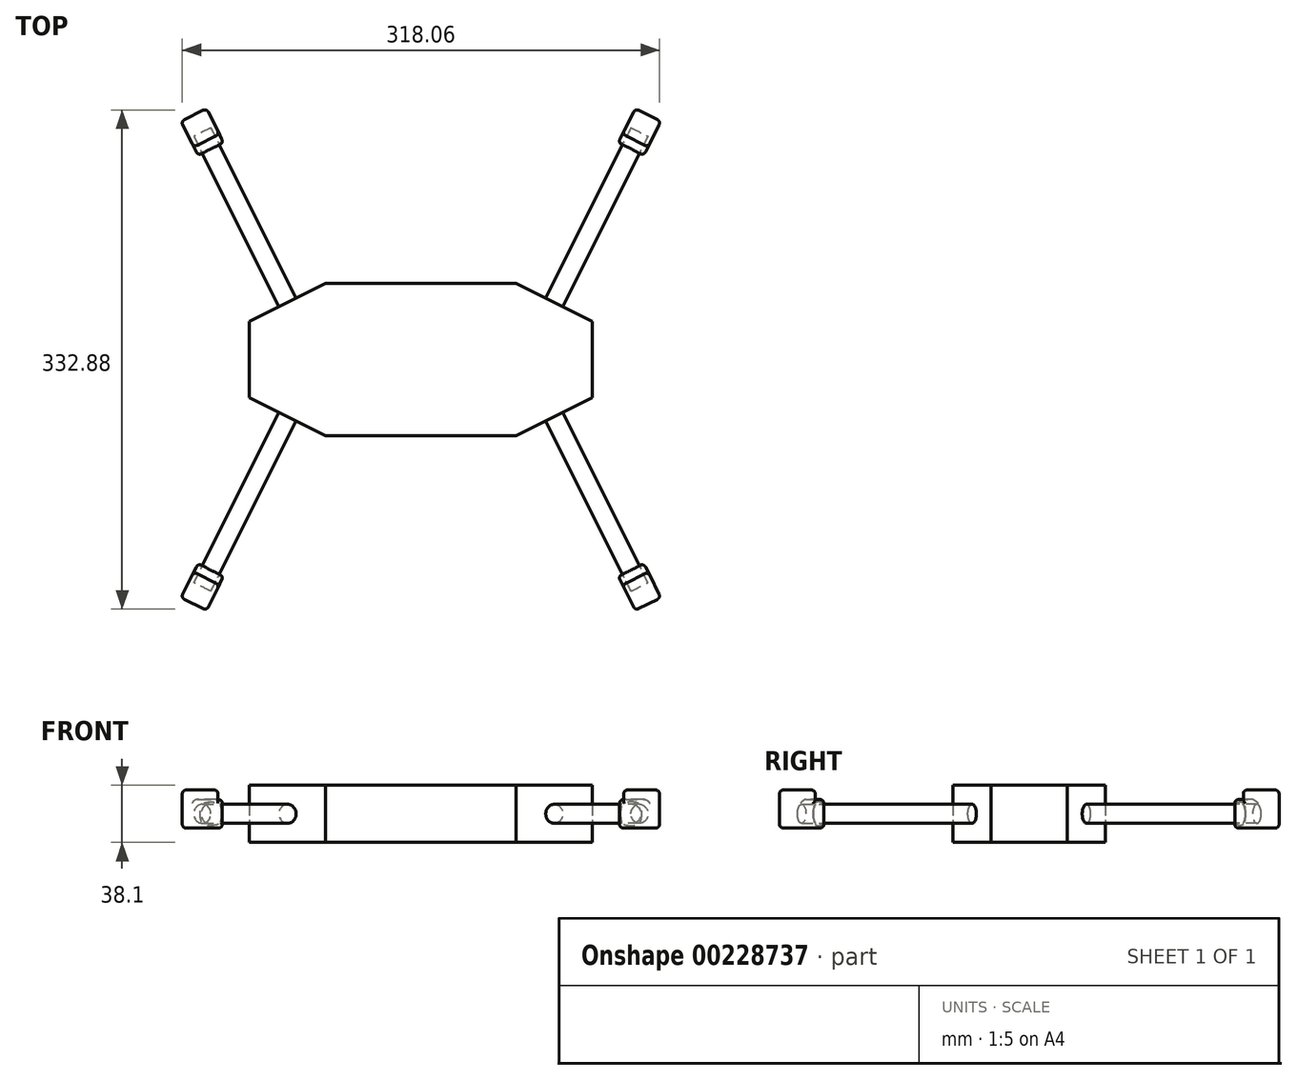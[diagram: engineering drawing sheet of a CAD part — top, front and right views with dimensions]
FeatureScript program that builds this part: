
annotation { "Feature Type Name" : "Feature", "Feature Type Description" : "" }
export const myFeature = defineFeature(function(context is Context, id is Id, definition is map)
    precondition{}
    {
        {
            var Q0;
            Q0=qCreatedBy(makeId("Top.planeOp"),FACE);
            var sketch = newSketch(context, id + "F0", { "sketchPlane" : qUnion([Q0])});
            skLineSegment(sketch, "E0.left", {"start": v(-114.3, 25.4) * mm, "end": v(-114.3, -25.4) * mm});
            skPoint(sketch, "E0.middle", {"position": v(0, 0) * mm});
            skLineSegment(sketch, "E1", {"start": v(-63.5, 50.8) * mm, "end": v(-114.3, 25.4) * mm});
            skLineSegment(sketch, "E2", {"start": v(-114.3, -25.4) * mm, "end": v(-63.5, -50.8) * mm});
            skLineSegment(sketch, "E3", {"start": v(0, 74.05) * mm, "end": v(0, -66) * mm, "construction": true});
            skLineSegment(sketch, "E4", {"start": v(-63.5, 50.8) * mm, "end": v(63.5, 50.8) * mm});
            skLineSegment(sketch, "E5", {"start": v(63.5, -50.8) * mm, "end": v(-63.5, -50.8) * mm});
            skLineSegment(sketch, "E6.MirrorCS", {"start": v(63.5, 50.8) * mm, "end": v(114.3, 25.4) * mm});
            skLineSegment(sketch, "E7.MirrorCS", {"start": v(114.3, 25.4) * mm, "end": v(114.3, -25.4) * mm});
            skLineSegment(sketch, "E8.MirrorCS", {"start": v(114.3, -25.4) * mm, "end": v(63.5, -50.8) * mm});
            skSolve(sketch);
        }
        {
            var Q0;
            Q0=makeQuery(id+"F0.imprint","IMPRINT",FACE,{"disambiguationData":[TD([[makeQuery(id+"F0.imprint","IMPRINT",EDGE,{"derivedFrom":sQuery(id+"F0.wireOp",EDGE,"E0.left")}),1.0]])]});
            extrude(context, id + "F1", {"entities" : qUnion([Q0]), "depth" : 38.1 * mm});
        }
        {
            var Q0;
            Q0=makeQuery(id+"F1.opExtrude","SWEPT_FACE",FACE,{"disambiguationData":[OSD([sQuery(id+"F0.wireOp",EDGE,"E2")])]});
            var sketch = newSketch(context, id + "F2", { "sketchPlane" : qUnion([Q0])});
            skLineSegment(sketch, "E9", {"start": v(-90.87, 38.1) * mm, "end": v(-34.08, 0) * mm, "construction": true});
            skLineSegment(sketch, "E10", {"start": v(-34.08, 38.1) * mm, "end": v(-90.87, 0) * mm, "construction": true});
            skCircle(sketch, "E11", {"center": v(-62.48, 19.05) * mm, "radius": 6.35 * mm});
            skSolve(sketch);
        }
        {
            var Q0;
            Q0=makeQuery(id+"F2.imprint","IMPRINT",FACE,{"disambiguationData":[TD([[makeQuery(id+"F2.imprint","IMPRINT",EDGE,{"derivedFrom":sQuery(id+"F2.wireOp",EDGE,"E11")}),1.0]])]});
            extrude(context, id + "F3", {"entities" : qUnion([Q0]), "depth" : 127 * mm});
        }
        {
            var Q0;
            Q0=makeQuery(id+"F3.opExtrude","CAP_FACE",FACE,{"disambiguationData":[OSD([sQuery(id+"F2.wireOp",EDGE,"E11")])],"isStart":false});
            var sketch = newSketch(context, id + "F4", { "sketchPlane" : qUnion([Q0])});
            skLineSegment(sketch, "E12.bottom", {"start": v(-72, 28.57) * mm, "end": v(-52.95, 28.57) * mm});
            skLineSegment(sketch, "E12.top", {"start": v(-72, 9.52) * mm, "end": v(-52.95, 9.52) * mm});
            skLineSegment(sketch, "E12.left", {"start": v(-72, 28.57) * mm, "end": v(-72, 9.52) * mm});
            skLineSegment(sketch, "E12.right", {"start": v(-52.95, 28.57) * mm, "end": v(-52.95, 9.52) * mm});
            skPoint(sketch, "E12.middle", {"position": v(-62.48, 19.05) * mm});
            skSolve(sketch);
        }
        {
            var Q0;
            Q0 = qSketchRegion(id + "F4", true);
            extrude(context, id + "F5", {"entities" : qUnion([Q0]), "endBound" : BoundingType.SYMMETRIC, "depth" : 25.4 * mm});
        }
        {
            var Q0;
            Q0=makeQuery(id+"F5.opExtrude","SWEPT_FACE",FACE,{"disambiguationData":[OSD([sQuery(id+"F4.wireOp",EDGE,"E12.bottom")])]});
            var sketch = newSketch(context, id + "F6", { "sketchPlane" : qUnion([Q0])});
            skLineSegment(sketch, "E13", {"start": v(-159.9, -158.8) * mm, "end": v(-142.86, -167.31) * mm});
            skLineSegment(sketch, "E14", {"start": v(-142.86, -167.31) * mm, "end": v(-134.34, -150.27) * mm});
            skLineSegment(sketch, "E15", {"start": v(-134.34, -150.27) * mm, "end": v(-151.38, -141.75) * mm});
            skLineSegment(sketch, "E16", {"start": v(-151.38, -141.75) * mm, "end": v(-159.9, -158.8) * mm});
            skSolve(sketch);
        }
        {
            var Q0;
            Q0=makeQuery(id+"F6.imprint","IMPRINT",FACE,{"disambiguationData":[TD([[makeQuery(id+"F6.imprint","IMPRINT",EDGE,{"derivedFrom":sQuery(id+"F6.wireOp",EDGE,"E13")}),1.0]])]});
            extrude(context, id + "F7", {"entities" : qUnion([Q0]), "operationType" : NewBodyOperationType.ADD, "depth" : 6.35 * mm});
        }
        {
            var Q0;
            Q0=makeQuery(id+"F3.opExtrude","SWEPT_BODY",BODY,{"disambiguationData":[OSD([sQuery(id+"F2.wireOp",EDGE,"E11")])]});
            var Q1;
            Q1=makeQuery(id+"F5.opExtrude","SWEPT_BODY",BODY,{"disambiguationData":[OSD([sQuery(id+"F4.wireOp",EDGE,"E12.bottom"),sQuery(id+"F4.wireOp",EDGE,"E12.top"),sQuery(id+"F4.wireOp",EDGE,"E12.left"),sQuery(id+"F4.wireOp",EDGE,"E12.right")])]});
            booleanBodies(context, id + "F8", {"operationType" : BooleanOperationType.SUBTRACTION, "tools" : qUnion([Q0]), "targets" : qUnion([Q1]), "keepTools" : true});
        }
        {
            var Q0;
            Q0=makeQuery(id+"F7.boolean.opBoolean","MERGE",FACE,{"derivedFrom":[makeQuery(id+"F5.opExtrude","SWEPT_FACE",FACE,{"disambiguationData":[OSD([sQuery(id+"F4.wireOp",EDGE,"E12.left")])]}),makeQuery(id+"F7.opExtrude","SWEPT_FACE",FACE,{"disambiguationData":[OSD([sQuery(id+"F6.wireOp",EDGE,"E16")])]})]});
            var Q1;
            Q1=makeQuery(id+"F7.opExtrude","CAP_FACE",FACE,{"disambiguationData":[OSD([sQuery(id+"F6.wireOp",EDGE,"E13"),sQuery(id+"F6.wireOp",EDGE,"E14"),sQuery(id+"F6.wireOp",EDGE,"E15"),sQuery(id+"F6.wireOp",EDGE,"E16")])],"isStart":false});
            var Q2;
            Q2=makeQuery(id+"F7.boolean.opBoolean","MERGE",FACE,{"derivedFrom":[makeQuery(id+"F5.opExtrude","SWEPT_FACE",FACE,{"disambiguationData":[OSD([sQuery(id+"F4.wireOp",EDGE,"E12.right")])]}),makeQuery(id+"F7.opExtrude","SWEPT_FACE",FACE,{"disambiguationData":[OSD([sQuery(id+"F6.wireOp",EDGE,"E14")])]})]});
            var Q3;
            Q3=makeQuery(id+"F7.boolean.opBoolean","MERGE",FACE,{"derivedFrom":[makeQuery(id+"F5.opExtrude","CAP_FACE",FACE,{"disambiguationData":[OSD([sQuery(id+"F4.wireOp",EDGE,"E12.bottom"),sQuery(id+"F4.wireOp",EDGE,"E12.top"),sQuery(id+"F4.wireOp",EDGE,"E12.left"),sQuery(id+"F4.wireOp",EDGE,"E12.right")])],"isStart":false}),makeQuery(id+"F7.opExtrude","SWEPT_FACE",FACE,{"disambiguationData":[OSD([sQuery(id+"F6.wireOp",EDGE,"E13")])]})]});
            var Q4;
            Q4=makeQuery(id+"F5.opExtrude","CAP_FACE",FACE,{"disambiguationData":[OSD([sQuery(id+"F4.wireOp",EDGE,"E12.bottom"),sQuery(id+"F4.wireOp",EDGE,"E12.top"),sQuery(id+"F4.wireOp",EDGE,"E12.left"),sQuery(id+"F4.wireOp",EDGE,"E12.right")])],"isStart":true});
            fillet(context, id + "F9", {"entities" : qUnion([Q0, Q1, Q2, Q3, Q4]), "radius" : 2.54 * mm, "tangentPropagation" : true, "allowEdgeOverflow" : false});
        }
        {
            var Q0;
            Q0=makeQuery(id+"F3.opExtrude","SWEPT_BODY",BODY,{"disambiguationData":[OSD([sQuery(id+"F2.wireOp",EDGE,"E11")])]});
            var Q1;
            Q1=makeQuery(id+"F5.opExtrude","SWEPT_BODY",BODY,{"disambiguationData":[OSD([sQuery(id+"F4.wireOp",EDGE,"E12.bottom"),sQuery(id+"F4.wireOp",EDGE,"E12.top"),sQuery(id+"F4.wireOp",EDGE,"E12.left"),sQuery(id+"F4.wireOp",EDGE,"E12.right")])]});
            var Q2;
            Q2=qCreatedBy(makeId("Right.planeOp"),FACE);
            mirror(context, id + "F10", {"entities" : qUnion([Q0, Q1]), "mirrorPlane" : qUnion([Q2])});
        }
        {
            var Q0;
            Q0=makeQuery(id+"F10.opPattern","COPY",BODY,{"derivedFrom":makeQuery(id+"F5.opExtrude","SWEPT_BODY",BODY,{"disambiguationData":[OSD([sQuery(id+"F4.wireOp",EDGE,"E12.bottom"),sQuery(id+"F4.wireOp",EDGE,"E12.top"),sQuery(id+"F4.wireOp",EDGE,"E12.left"),sQuery(id+"F4.wireOp",EDGE,"E12.right")])]}),"instanceName":"1"});
            var Q1;
            Q1=makeQuery(id+"F10.opPattern","COPY",BODY,{"derivedFrom":makeQuery(id+"F3.opExtrude","SWEPT_BODY",BODY,{"disambiguationData":[OSD([sQuery(id+"F2.wireOp",EDGE,"E11")])]}),"instanceName":"1"});
            var Q2;
            Q2=makeQuery(id+"F3.opExtrude","SWEPT_BODY",BODY,{"disambiguationData":[OSD([sQuery(id+"F2.wireOp",EDGE,"E11")])]});
            var Q3;
            Q3=makeQuery(id+"F5.opExtrude","SWEPT_BODY",BODY,{"disambiguationData":[OSD([sQuery(id+"F4.wireOp",EDGE,"E12.bottom"),sQuery(id+"F4.wireOp",EDGE,"E12.top"),sQuery(id+"F4.wireOp",EDGE,"E12.left"),sQuery(id+"F4.wireOp",EDGE,"E12.right")])]});
            var Q4;
            Q4=qCreatedBy(makeId("Front.planeOp"),FACE);
            mirror(context, id + "F11", {"entities" : qUnion([Q0, Q1, Q2, Q3]), "mirrorPlane" : qUnion([Q4])});
        }
    });
